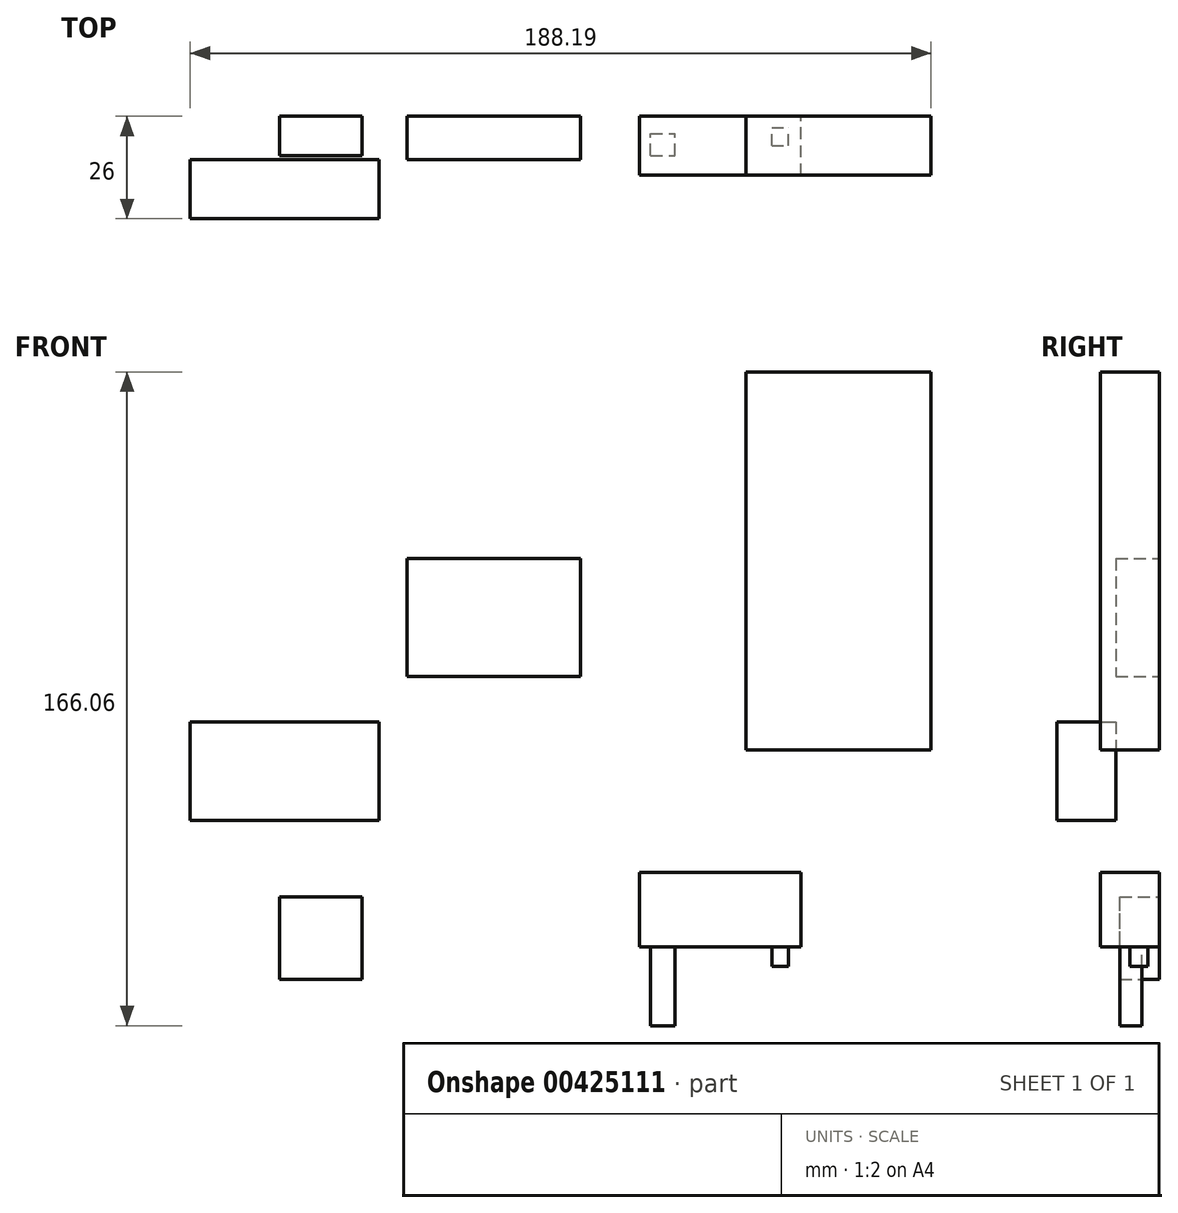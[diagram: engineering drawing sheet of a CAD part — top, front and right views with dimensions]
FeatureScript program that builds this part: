
annotation { "Feature Type Name" : "Feature", "Feature Type Description" : "" }
export const myFeature = defineFeature(function(context is Context, id is Id, definition is map)
    precondition{}
    {
        {
            var Q0;
            Q0=qCreatedBy(makeId("Front.planeOp"),FACE);
            var sketch = newSketch(context, id + "F0", { "sketchPlane" : qUnion([Q0])});
            skLineSegment(sketch, "E0.bottom", {"start": v(0, 0) * mm, "end": v(47, 0) * mm});
            skLineSegment(sketch, "E0.top", {"start": v(0, 96) * mm, "end": v(47, 96) * mm});
            skLineSegment(sketch, "E0.left", {"start": v(0, 0) * mm, "end": v(0, 96) * mm});
            skLineSegment(sketch, "E0.right", {"start": v(47, 0) * mm, "end": v(47, 96) * mm});
            skSolve(sketch);
        }
        {
            var Q0;
            Q0 = qSketchRegion(id + "F0", true);
            extrude(context, id + "F1", {"entities" : qUnion([Q0]), "depth" : 15 * mm});
        }
        {
            var Q0;
            Q0=qCreatedBy(makeId("Front.planeOp"),FACE);
            var sketch = newSketch(context, id + "F2", { "sketchPlane" : qUnion([Q0])});
            skLineSegment(sketch, "E1.bottom", {"start": v(-86.06, 48.6) * mm, "end": v(-42.06, 48.6) * mm});
            skLineSegment(sketch, "E1.top", {"start": v(-86.06, 18.6) * mm, "end": v(-42.06, 18.6) * mm});
            skLineSegment(sketch, "E1.left", {"start": v(-86.06, 48.6) * mm, "end": v(-86.06, 18.6) * mm});
            skLineSegment(sketch, "E1.right", {"start": v(-42.06, 48.6) * mm, "end": v(-42.06, 18.6) * mm});
            skSolve(sketch);
        }
        {
            var Q0;
            Q0 = qSketchRegion(id + "F2", true);
            extrude(context, id + "F3", {"entities" : qUnion([Q0]), "depth" : 11 * mm});
        }
        {
            var Q0;
            Q0=makeQuery(id+"F3.opExtrude","CAP_FACE",FACE,{"disambiguationData":[OSD([sQuery(id+"F2.wireOp",EDGE,"E1.bottom"),sQuery(id+"F2.wireOp",EDGE,"E1.top"),sQuery(id+"F2.wireOp",EDGE,"E1.left"),sQuery(id+"F2.wireOp",EDGE,"E1.right")])],"isStart":false});
            var sketch = newSketch(context, id + "F4", { "sketchPlane" : qUnion([Q0])});
            skLineSegment(sketch, "E2.bottom", {"start": v(-141.19, 7.08) * mm, "end": v(-93.19, 7.08) * mm});
            skLineSegment(sketch, "E2.top", {"start": v(-141.19, -17.92) * mm, "end": v(-93.19, -17.92) * mm});
            skLineSegment(sketch, "E2.left", {"start": v(-141.19, 7.08) * mm, "end": v(-141.19, -17.92) * mm});
            skLineSegment(sketch, "E2.right", {"start": v(-93.19, 7.08) * mm, "end": v(-93.19, -17.92) * mm});
            skSolve(sketch);
        }
        {
            var Q0;
            Q0=makeQuery(id+"F4.imprint","IMPRINT",FACE,{"disambiguationData":[TD([[makeQuery(id+"F4.imprint","IMPRINT",EDGE,{"derivedFrom":sQuery(id+"F4.wireOp",EDGE,"E2.bottom")}),-1.0]])]});
            extrude(context, id + "F5", {"entities" : qUnion([Q0]), "depth" : 15 * mm});
        }
        {
            var Q0;
            Q0=qCreatedBy(makeId("Front.planeOp"),FACE);
            var sketch = newSketch(context, id + "F6", { "sketchPlane" : qUnion([Q0])});
            skLineSegment(sketch, "E3.bottom", {"start": v(-118.54, -58.32) * mm, "end": v(-97.54, -58.32) * mm});
            skLineSegment(sketch, "E3.top", {"start": v(-118.54, -37.32) * mm, "end": v(-97.54, -37.32) * mm});
            skLineSegment(sketch, "E3.left", {"start": v(-118.54, -58.32) * mm, "end": v(-118.54, -37.32) * mm});
            skLineSegment(sketch, "E3.right", {"start": v(-97.54, -58.32) * mm, "end": v(-97.54, -37.32) * mm});
            skSolve(sketch);
        }
        {
            var Q0;
            Q0=makeQuery(id+"F6.imprint","IMPRINT",FACE,{"disambiguationData":[TD([[makeQuery(id+"F6.imprint","IMPRINT",EDGE,{"derivedFrom":sQuery(id+"F6.wireOp",EDGE,"E3.bottom")}),1.0]])]});
            extrude(context, id + "F7", {"entities" : qUnion([Q0]), "depth" : 10 * mm});
        }
        {
            var Q0;
            Q0=qCreatedBy(makeId("Front.planeOp"),FACE);
            var sketch = newSketch(context, id + "F8", { "sketchPlane" : qUnion([Q0])});
            skLineSegment(sketch, "E4.bottom", {"start": v(-27.01, -31.06) * mm, "end": v(13.99, -31.06) * mm});
            skLineSegment(sketch, "E4.top", {"start": v(-27.01, -50.06) * mm, "end": v(13.99, -50.06) * mm});
            skLineSegment(sketch, "E4.left", {"start": v(-27.01, -31.06) * mm, "end": v(-27.01, -50.06) * mm});
            skLineSegment(sketch, "E4.right", {"start": v(13.99, -31.06) * mm, "end": v(13.99, -50.06) * mm});
            skSolve(sketch);
        }
        {
            var Q0;
            Q0 = qSketchRegion(id + "F8", true);
            extrude(context, id + "F9", {"entities" : qUnion([Q0]), "depth" : 15 * mm});
        }
        {
            var Q0;
            Q0=makeQuery(id+"F9.opExtrude","SWEPT_FACE",FACE,{"disambiguationData":[OSD([sQuery(id+"F8.wireOp",EDGE,"E4.top")])]});
            var sketch = newSketch(context, id + "F10", { "sketchPlane" : qUnion([Q0])});
            skLineSegment(sketch, "E5.bottom", {"start": v(-24.2, 9.98) * mm, "end": v(-18.03, 9.98) * mm});
            skLineSegment(sketch, "E5.top", {"start": v(-24.2, 4.35) * mm, "end": v(-18.03, 4.35) * mm});
            skLineSegment(sketch, "E5.left", {"start": v(-24.2, 9.98) * mm, "end": v(-24.2, 4.35) * mm});
            skLineSegment(sketch, "E5.right", {"start": v(-18.03, 9.98) * mm, "end": v(-18.03, 4.35) * mm});
            skPoint(sketch, "E6.firstSnap0", {"position": v(13.99, 7.5) * mm});
            skLineSegment(sketch, "E6.bottom", {"start": v(6.6, 7.5) * mm, "end": v(10.8, 7.5) * mm});
            skLineSegment(sketch, "E6.top", {"start": v(6.6, 2.86) * mm, "end": v(10.8, 2.86) * mm});
            skLineSegment(sketch, "E6.left", {"start": v(6.6, 7.5) * mm, "end": v(6.6, 2.86) * mm});
            skLineSegment(sketch, "E6.right", {"start": v(10.8, 7.5) * mm, "end": v(10.8, 2.86) * mm});
            skSolve(sketch);
        }
        {
            var Q0;
            Q0=makeQuery(id+"F10.imprint","IMPRINT",FACE,{"disambiguationData":[TD([[makeQuery(id+"F10.imprint","IMPRINT",EDGE,{"derivedFrom":sQuery(id+"F10.wireOp",EDGE,"E5.bottom")}),-1.0]])]});
            extrude(context, id + "F11", {"entities" : qUnion([Q0]), "operationType" : NewBodyOperationType.ADD, "depth" : 20 * mm});
        }
        {
            var Q0;
            Q0=makeQuery(id+"F10.imprint","IMPRINT",FACE,{"disambiguationData":[TD([[makeQuery(id+"F10.imprint","IMPRINT",EDGE,{"derivedFrom":sQuery(id+"F10.wireOp",EDGE,"E6.bottom")}),-1.0]])]});
            extrude(context, id + "F12", {"entities" : qUnion([Q0]), "operationType" : NewBodyOperationType.ADD, "depth" : 5 * mm});
        }
    });
